# Revit family: Electronics_Desono_Biamp_Two-Way-Conferencing-Loudspeaker_C-IC6LP
name_source: partatom
category: Communication Devices
units: mm (PartAtom-declared; Revit-internal decimal feet)

## family parameters
Cut with Voids When Loaded = No
Host = Face
Maintain Annotation Orientation = No
OmniClass Number = 23.85.10.11.14.14.14
OmniClass Title = Loudspeakers
Part Type = Normal
Room Calculation Point = No
Round Connector Dimension = Use Diameter
Shared = No

## types (8) — shared parameters
Certifcations = ETL listed to comply with UL1480A, UL2043 and CSA62368-1 Suitable for use in air handling spaces per NFPA 70 and NFPA 90
Connector Description = 4-pole Euroblock; 22V 60W 8Ω (240W peak)
Crossover Frequency = 2.5 kHz
Default Elevation = 48 "
Depth = 4 "
Description = Desono™ C-IC6LP Two-Way 6.5 Ceiling Mount Conferencing Loudspeaker
Diameter = 13 "
Input Connection = 4-position Euroblock connector, 2 RJ45 ports
Manufacturer = Biamp
Mounting Provisions = 3 SpringLock™ mounting clamps with 33 mm (1.3) grip range
Nominal Beamwidth  (H x V) = 130°, conical
Nominal Continuous Power Handling = 22 V (60 W @ 8 Ω)
Nominal Maximum SPL = Peak - 109dB; Continuous -103dB
Operating Environment = Indoor in climate-controlled environments
Operating Mode = Passive with DSP
Operating Range (-10dB) = Indoor
Product Documentation Link = https://downloads.biamp.com
Product Page URL = https://www.biamp.com
Product data url = https://bimobject.com
Rated Continuous Voltage = 21.9 V (27 dBV)
Rated Maximum SPL (Processed) = Peak - 115dB; Continuous -103dB
Recommended Amplifers = 60 W - 120 W into 8 Ω, (22 V - 31 V)
Required Accessory = 65 Hz, 18 dB/oct. high pass flter; DSP preset for ALC or Tesira
Sensitivity = 87 dB (2.83 V);87 dB (1 W at rated impedance 8 Ω)
Shipping Weight = 27.11 lb
Transducers = LF 1 x 6.5 (165 mm) treated paper cone; HF 1 x 1 (25 mm) soft dome
URL = https://www.biamp.com
Version = 1
Weight = 9.10 lb
connector = No

## per-type parameters (varying)
| type | ABP450 | Connector 450 | Connector X | Connector XA | Grill Material | Housing Material | TCM-X | TCM-XA |
| C-IC6LP-W | No | 2 | 2 | 2 | Biamp - Plastic - White(Grid) | Biamp - Metal - White | No | No |
| C-IC6LP-W with Amp-450BP | Yes | 3 | 2 | 2 | Biamp - Plastic - White(Grid) | Biamp - Metal - White | No | No |
| C-IC6LP-W with TCM-X | No | 2 | 3 | 2 | Biamp - Plastic - White(Grid) | Biamp - Metal - White | Yes | No |
| C-IC6LP-W with TCM-XA | No | 2 | 2 | 3 | Biamp - Plastic - White(Grid) | Biamp - Metal - White | No | Yes |
| C-IC6LP-B | No | 2 | 2 | 2 | Biamp - Plastic - Black(Grid) | Biamp - Metal - Black | No | No |
| C-IC6LP-B with Amp-450BP | Yes | 3 | 2 | 2 | Biamp - Plastic - Black(Grid) | Biamp - Metal - Black | No | No |
| C-IC6LP-B with TCM-X | No | 2 | 3 | 2 | Biamp - Plastic - Black(Grid) | Biamp - Metal - Black | Yes | No |
| C-IC6LP-B with TCM-XA | No | 2 | 2 | 3 | Biamp - Plastic - Black(Grid) | Biamp - Metal - Black | No | Yes |

note: column(s) folded — value = type name in every type: Model

## geometry (parser evidence)
native form markers: Sweep x4
no freeform markers — native parametric forms only
